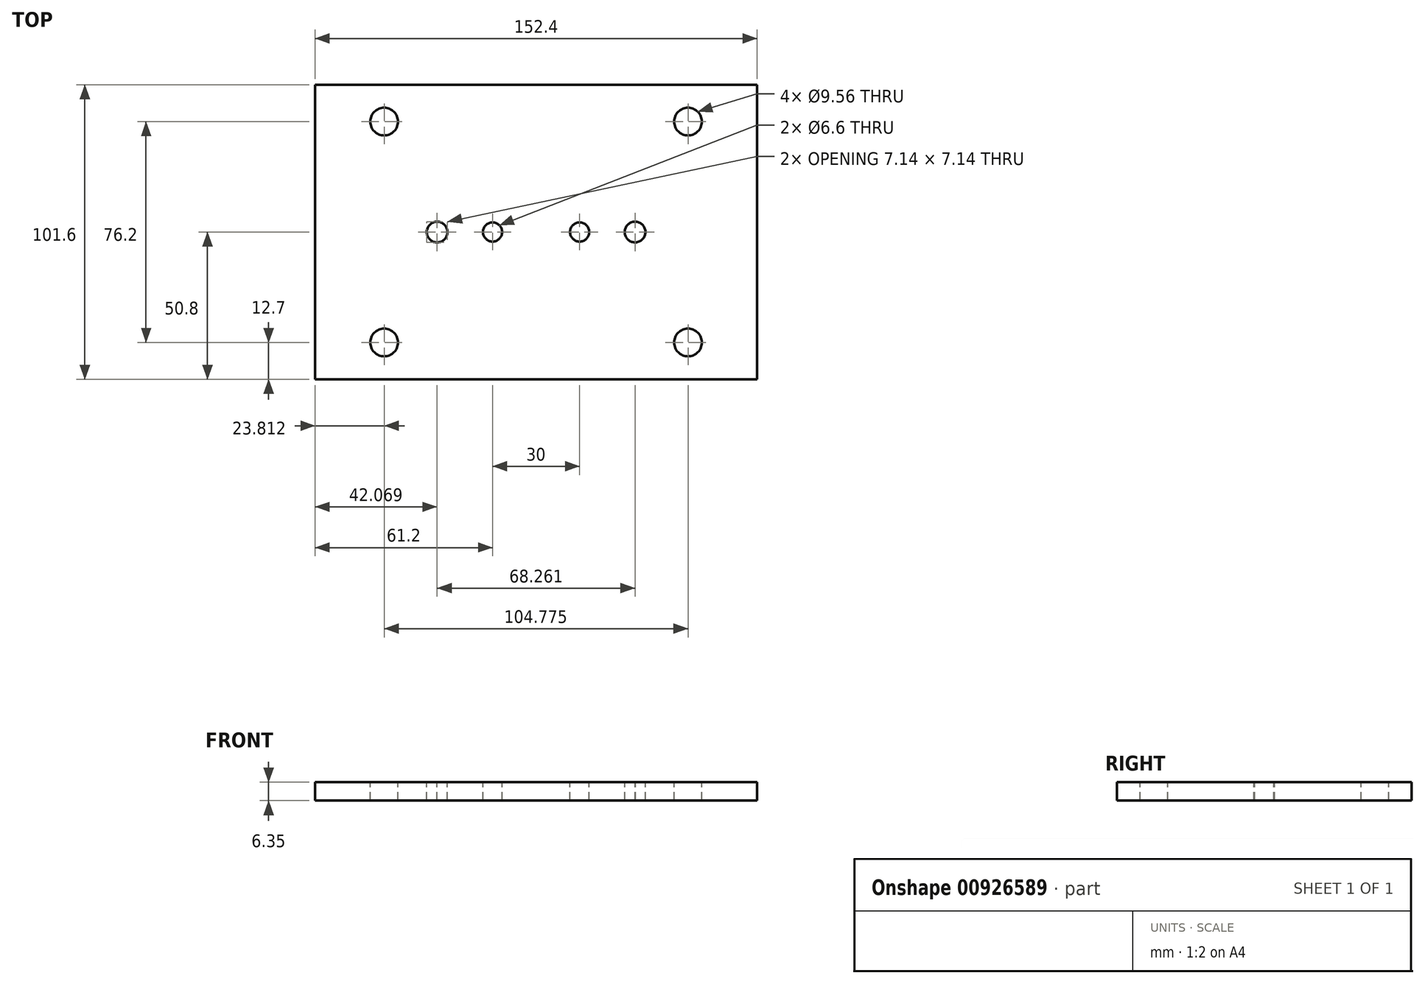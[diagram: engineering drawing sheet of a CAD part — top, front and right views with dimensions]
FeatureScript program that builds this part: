
annotation { "Feature Type Name" : "Feature", "Feature Type Description" : "" }
export const myFeature = defineFeature(function(context is Context, id is Id, definition is map)
    precondition{}
    {
        {
            var Q0;
            Q0=qCreatedBy(makeId("Top.planeOp"),FACE);
            var sketch = newSketch(context, id + "F0", { "sketchPlane" : qUnion([Q0])});
            skLineSegment(sketch, "E0.bottom", {"start": v(-76.2, 50.8) * mm, "end": v(76.2, 50.8) * mm});
            skLineSegment(sketch, "E0.top", {"start": v(-76.2, -50.8) * mm, "end": v(76.2, -50.8) * mm});
            skLineSegment(sketch, "E0.left", {"start": v(-76.2, 50.8) * mm, "end": v(-76.2, -50.8) * mm});
            skLineSegment(sketch, "E0.right", {"start": v(76.2, 50.8) * mm, "end": v(76.2, -50.8) * mm});
            skLineSegment(sketch, "E1", {"start": v(-76.2, 0) * mm, "end": v(0, 0) * mm, "construction": true});
            skLineSegment(sketch, "E2", {"start": v(0, 0) * mm, "end": v(76.2, 0) * mm, "construction": true});
            skLineSegment(sketch, "E3", {"start": v(0, 50.8) * mm, "end": v(0, 0) * mm, "construction": true});
            skLineSegment(sketch, "E4", {"start": v(0, 0) * mm, "end": v(0, -50.8) * mm, "construction": true});
            skSolve(sketch);
        }
        {
            var Q0;
            Q0 = qSketchRegion(id + "F0", true);
            extrude(context, id + "F1", {"entities" : qUnion([Q0]), "depth" : 6.35 * mm, "offsetDistance" : 25.4 * mm});
        }
        {
            var Q0;
            Q0=makeQuery(id+"F1.opExtrude","CAP_FACE",FACE,{"disambiguationData":[OSD([sQuery(id+"F0.wireOp",EDGE,"E0.bottom"),sQuery(id+"F0.wireOp",EDGE,"E0.top"),sQuery(id+"F0.wireOp",EDGE,"E0.left"),sQuery(id+"F0.wireOp",EDGE,"E0.right")])],"isStart":false});
            var sketch = newSketch(context, id + "F2", { "sketchPlane" : qUnion([Q0])});
            skCircle(sketch, "E5", {"center": v(-52.39, 38.1) * mm, "radius": 4.78 * mm});
            skCircle(sketch, "E6.0.1.0", {"center": v(-52.39, -38.1) * mm, "radius": 4.78 * mm});
            skCircle(sketch, "E6.1.0.0", {"center": v(52.39, 38.1) * mm, "radius": 4.78 * mm});
            skCircle(sketch, "E6.1.1.0", {"center": v(52.39, -38.1) * mm, "radius": 4.78 * mm});
            skLineSegment(sketch, "E6.direction1", {"start": v(-52.39, 38.1) * mm, "end": v(52.39, 38.1) * mm, "construction": true});
            skLineSegment(sketch, "E6.direction2", {"start": v(-52.39, 38.1) * mm, "end": v(-52.39, -38.1) * mm, "construction": true});
            skLineSegment(sketch, "E7", {"start": v(-52.39, 38.1) * mm, "end": v(-76.2, 38.1) * mm, "construction": true});
            skLineSegment(sketch, "E8", {"start": v(52.39, 38.1) * mm, "end": v(76.2, 38.1) * mm, "construction": true});
            skLineSegment(sketch, "E9", {"start": v(-52.39, 38.1) * mm, "end": v(-52.39, 50.8) * mm, "construction": true});
            skLineSegment(sketch, "E10", {"start": v(-52.39, -38.1) * mm, "end": v(-52.39, -50.8) * mm, "construction": true});
            skSolve(sketch);
        }
        {
            var Q0;
            Q0=makeQuery(id+"F2.imprint","IMPRINT",FACE,{"disambiguationData":[TD([[makeQuery(id+"F2.imprint","IMPRINT",EDGE,{"derivedFrom":sQuery(id+"F2.wireOp",EDGE,"E5")}),1.0]])]});
            var Q1;
            Q1=makeQuery(id+"F2.imprint","IMPRINT",FACE,{"disambiguationData":[TD([[makeQuery(id+"F2.imprint","IMPRINT",EDGE,{"derivedFrom":sQuery(id+"F2.wireOp",EDGE,"E6.1.0.0")}),1.0]])]});
            var Q2;
            Q2=makeQuery(id+"F2.imprint","IMPRINT",FACE,{"disambiguationData":[TD([[makeQuery(id+"F2.imprint","IMPRINT",EDGE,{"derivedFrom":sQuery(id+"F2.wireOp",EDGE,"E6.0.1.0")}),1.0]])]});
            var Q3;
            Q3=makeQuery(id+"F2.imprint","IMPRINT",FACE,{"disambiguationData":[TD([[makeQuery(id+"F2.imprint","IMPRINT",EDGE,{"derivedFrom":sQuery(id+"F2.wireOp",EDGE,"E6.1.1.0")}),1.0]])]});
            extrude(context, id + "F3", {"entities" : qUnion([Q0, Q1, Q2, Q3]), "operationType" : NewBodyOperationType.REMOVE, "endBound" : BoundingType.UP_TO_NEXT, "oppositeDirection" : true, "depth" : 25.4 * mm, "offsetDistance" : 25.4 * mm});
        }
        {
            var Q0;
            Q0=makeQuery(id+"F1.opExtrude","CAP_FACE",FACE,{"disambiguationData":[OSD([sQuery(id+"F0.wireOp",EDGE,"E0.bottom"),sQuery(id+"F0.wireOp",EDGE,"E0.top"),sQuery(id+"F0.wireOp",EDGE,"E0.left"),sQuery(id+"F0.wireOp",EDGE,"E0.right")])],"isStart":false});
            var sketch = newSketch(context, id + "F4", { "sketchPlane" : qUnion([Q0])});
            skArc(sketch, "E11", {"start": v(-34.13, -3.57) * mm, "mid": v(-34.09, 3.57) * mm, "end": v(-34.22, -3.57) * mm});
            skArc(sketch, "E12", {"start": v(34.28, -3.57) * mm, "mid": v(34.06, 3.57) * mm, "end": v(34.13, -3.57) * mm});
            skLineSegment(sketch, "E13", {"start": v(-34.13, 0) * mm, "end": v(0, 0) * mm, "construction": true});
            skLineSegment(sketch, "E14", {"start": v(0, 0) * mm, "end": v(34.13, 0) * mm, "construction": true});
            skLineSegment(sketch, "E15", {"start": v(-34.22, -3.57) * mm, "end": v(-34.13, -3.57) * mm});
            skLineSegment(sketch, "E16", {"start": v(34.13, -3.57) * mm, "end": v(34.28, -3.57) * mm});
            skSolve(sketch);
        }
        {
            var Q0;
            Q0=makeQuery(id+"F4.imprint","IMPRINT",FACE,{"disambiguationData":[TD([[makeQuery(id+"F4.imprint","IMPRINT",EDGE,{"derivedFrom":sQuery(id+"F4.wireOp",EDGE,"E11")}),1.0]])]});
            var Q1;
            Q1=makeQuery(id+"F4.imprint","IMPRINT",FACE,{"disambiguationData":[TD([[makeQuery(id+"F4.imprint","IMPRINT",EDGE,{"derivedFrom":sQuery(id+"F4.wireOp",EDGE,"E12")}),1.0]])]});
            extrude(context, id + "F5", {"entities" : qUnion([Q0, Q1]), "operationType" : NewBodyOperationType.REMOVE, "endBound" : BoundingType.THROUGH_ALL, "oppositeDirection" : true, "depth" : 25.4 * mm, "offsetDistance" : 25.4 * mm});
        }
        {
            var Q0;
            Q0=makeQuery(id+"F1.opExtrude","CAP_FACE",FACE,{"disambiguationData":[OSD([sQuery(id+"F0.wireOp",EDGE,"E0.bottom"),sQuery(id+"F0.wireOp",EDGE,"E0.top"),sQuery(id+"F0.wireOp",EDGE,"E0.left"),sQuery(id+"F0.wireOp",EDGE,"E0.right")])],"isStart":false});
            var sketch = newSketch(context, id + "F6", { "sketchPlane" : qUnion([Q0])});
            skCircle(sketch, "E17", {"center": v(-15, 0) * mm, "radius": 3.3 * mm});
            skCircle(sketch, "E18", {"center": v(15, 0) * mm, "radius": 3.3 * mm});
            skLineSegment(sketch, "E19", {"start": v(-15, 0) * mm, "end": v(0, 0) * mm, "construction": true});
            skLineSegment(sketch, "E20", {"start": v(0, 0) * mm, "end": v(15, 0) * mm, "construction": true});
            skSolve(sketch);
        }
        {
            var Q0;
            Q0=makeQuery(id+"F6.imprint","IMPRINT",FACE,{"disambiguationData":[TD([[makeQuery(id+"F6.imprint","IMPRINT",EDGE,{"derivedFrom":sQuery(id+"F6.wireOp",EDGE,"E17")}),1.0]])]});
            var Q1;
            Q1=makeQuery(id+"F6.imprint","IMPRINT",FACE,{"disambiguationData":[TD([[makeQuery(id+"F6.imprint","IMPRINT",EDGE,{"derivedFrom":sQuery(id+"F6.wireOp",EDGE,"E18")}),1.0]])]});
            extrude(context, id + "F7", {"entities" : qUnion([Q0, Q1]), "operationType" : NewBodyOperationType.REMOVE, "endBound" : BoundingType.THROUGH_ALL, "oppositeDirection" : true, "depth" : 25.4 * mm, "offsetDistance" : 25.4 * mm});
        }
    });
